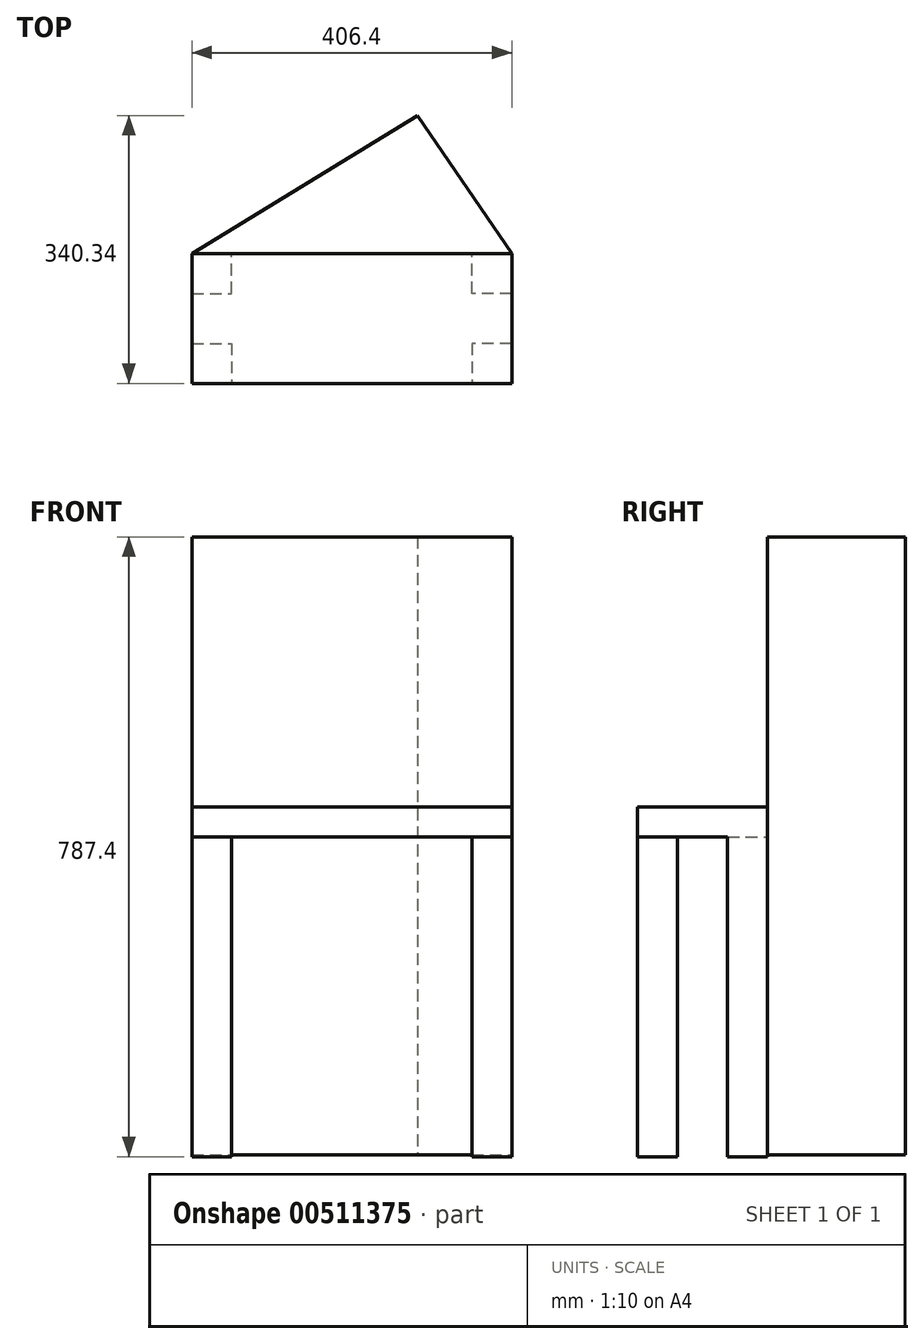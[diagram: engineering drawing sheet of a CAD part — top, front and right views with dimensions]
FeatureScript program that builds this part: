
annotation { "Feature Type Name" : "Feature", "Feature Type Description" : "" }
export const myFeature = defineFeature(function(context is Context, id is Id, definition is map)
    precondition{}
    {
        {
            var Q0;
            Q0=qCreatedBy(makeId("Top.planeOp"),FACE);
            var sketch = newSketch(context, id + "F0", { "sketchPlane" : qUnion([Q0])});
            skLineSegment(sketch, "E0", {"start": v(0, 0) * mm, "end": v(0, 50.8) * mm});
            skLineSegment(sketch, "E1", {"start": v(0, 50.8) * mm, "end": v(50.8, 50.8) * mm});
            skLineSegment(sketch, "E2", {"start": v(50.8, 50.8) * mm, "end": v(50.8, 0) * mm});
            skLineSegment(sketch, "E3", {"start": v(50.8, 0) * mm, "end": v(0, 0) * mm});
            skSolve(sketch);
        }
        {
            var Q0;
            Q0 = qSketchRegion(id + "F0", true);
            extrude(context, id + "F1", {"entities" : qUnion([Q0]), "depth" : 406.4 * mm});
        }
        {
            var Q0;
            Q0=makeQuery(id+"F1.opExtrude","CAP_FACE",FACE,{"disambiguationData":[OSD([sQuery(id+"F0.wireOp",EDGE,"E0"),sQuery(id+"F0.wireOp",EDGE,"E1"),sQuery(id+"F0.wireOp",EDGE,"E2"),sQuery(id+"F0.wireOp",EDGE,"E3")])],"isStart":false});
            var sketch = newSketch(context, id + "F2", { "sketchPlane" : qUnion([Q0])});
            skLineSegment(sketch, "E4", {"start": v(0, 0) * mm, "end": v(406.4, 0) * mm});
            skPoint(sketch, "E4.endSnap0", {"position": v(25.4, 0) * mm});
            skLineSegment(sketch, "E5", {"start": v(0, 0) * mm, "end": v(0, 164.9) * mm});
            skLineSegment(sketch, "E6", {"start": v(0, 164.9) * mm, "end": v(406.4, 164.9) * mm});
            skLineSegment(sketch, "E7", {"start": v(406.4, 164.9) * mm, "end": v(406.4, 0) * mm});
            skLineSegment(sketch, "E8", {"start": v(203.2, 164.9) * mm, "end": v(203.2, 0) * mm});
            skLineSegment(sketch, "E9", {"start": v(406.4, 82.45) * mm, "end": v(0, 82.45) * mm});
            skSolve(sketch);
        }
        {
            var Q0;
            Q0=sQuery(id+"F2.wireOp",EDGE,"E8");
            cPlane(context, id + "F3", {"entities" : qUnion([Q0]), "cplaneType" : CPlaneType.LINE_ANGLE, "offset" : 25.4 * mm, "angle" : 90 * degree, "width" : 152.4 * mm, "height" : 152.4 * mm});
        }
        {
            var Q0;
            Q0=sQuery(id+"F2.wireOp",EDGE,"E9");
            cPlane(context, id + "F4", {"entities" : qUnion([Q0]), "cplaneType" : CPlaneType.LINE_ANGLE, "offset" : 25.4 * mm, "angle" : 0 * degree, "width" : 152.4 * mm, "height" : 152.4 * mm});
        }
        {
            var Q0;
            Q0=makeQuery(id+"F1.opExtrude","SWEPT_BODY",BODY,{"disambiguationData":[OSD([sQuery(id+"F0.wireOp",EDGE,"E0"),sQuery(id+"F0.wireOp",EDGE,"E1"),sQuery(id+"F0.wireOp",EDGE,"E2"),sQuery(id+"F0.wireOp",EDGE,"E3")])]});
            var Q1;
            Q1=qCreatedBy(id+"F4.planeOp",FACE);
            mirror(context, id + "F5", {"entities" : qUnion([Q0]), "mirrorPlane" : qUnion([Q1])});
        }
        {
            var Q0;
            Q0=makeQuery(id+"F5.opPattern","COPY",BODY,{"derivedFrom":makeQuery(id+"F1.opExtrude","SWEPT_BODY",BODY,{"disambiguationData":[OSD([sQuery(id+"F0.wireOp",EDGE,"E0"),sQuery(id+"F0.wireOp",EDGE,"E1"),sQuery(id+"F0.wireOp",EDGE,"E2"),sQuery(id+"F0.wireOp",EDGE,"E3")])]}),"instanceName":"1"});
            var Q1;
            Q1=makeQuery(id+"F1.opExtrude","SWEPT_BODY",BODY,{"disambiguationData":[OSD([sQuery(id+"F0.wireOp",EDGE,"E0"),sQuery(id+"F0.wireOp",EDGE,"E1"),sQuery(id+"F0.wireOp",EDGE,"E2"),sQuery(id+"F0.wireOp",EDGE,"E3")])]});
            var Q2;
            Q2=qCreatedBy(id+"F3.planeOp",FACE);
            mirror(context, id + "F6", {"entities" : qUnion([Q0, Q1]), "mirrorPlane" : qUnion([Q2])});
        }
        {
            var Q0;
            {var subQ0=sQuery(id+"F2.wireOp",EDGE,"E7");var subQ1=sQuery(id+"F2.wireOp",EDGE,"E4");var subQ2=makeQuery(id+"F2.imprint","INTERSECT",VERTEX,{"derivedFrom":[subQ1,subQ0]});Q0=makeQuery(id+"F2.imprint","IMPRINT",FACE,{"disambiguationData":[TD([[makeQuery(id+"F2.imprint","IMPRINT",EDGE,{"disambiguationData":[TD([[subQ2,1.0]])],"derivedFrom":subQ1}),1.0]])]});}
            var Q1;
            {var subQ0=sQuery(id+"F2.wireOp",EDGE,"E6");var subQ1=sQuery(id+"F2.wireOp",EDGE,"E5");var subQ2=makeQuery(id+"F2.imprint","INTERSECT",VERTEX,{"derivedFrom":[subQ1,subQ0]});Q1=makeQuery(id+"F2.imprint","IMPRINT",FACE,{"disambiguationData":[TD([[makeQuery(id+"F2.imprint","IMPRINT",EDGE,{"disambiguationData":[TD([[subQ2,1.0]])],"derivedFrom":subQ1}),-1.0]])]});}
            var Q2;
            {var subQ5=makeQuery(id+"F1.opExtrude","CAP_EDGE",EDGE,{"disambiguationData":[OSD([sQuery(id+"F0.wireOp",EDGE,"E1")])],"isStart":false});Q2=makeQuery(id+"F2.imprint","IMPRINT",FACE,{"disambiguationData":[TD([[makeQuery(id+"F2.imprint","IMPRINT",EDGE,{"derivedFrom":subQ5}),1.0]])]});}
            var Q3;
            {var subQ0=sQuery(id+"F2.wireOp",EDGE,"E7");var subQ1=sQuery(id+"F2.wireOp",EDGE,"E6");var subQ2=makeQuery(id+"F2.imprint","INTERSECT",VERTEX,{"derivedFrom":[subQ1,subQ0]});Q3=makeQuery(id+"F2.imprint","IMPRINT",FACE,{"disambiguationData":[TD([[makeQuery(id+"F2.imprint","IMPRINT",EDGE,{"disambiguationData":[TD([[subQ2,1.0]])],"derivedFrom":subQ1}),-1.0]])]});}
            var Q4;
            {var subQ4=makeQuery(id+"F1.opExtrude","CAP_EDGE",EDGE,{"disambiguationData":[OSD([sQuery(id+"F0.wireOp",EDGE,"E1")])],"isStart":false});Q4=makeQuery(id+"F2.imprint","IMPRINT",FACE,{"disambiguationData":[TD([[makeQuery(id+"F2.imprint","IMPRINT",EDGE,{"derivedFrom":subQ4}),-1.0]])]});}
            extrude(context, id + "F7", {"entities" : qUnion([Q0, Q1, Q2, Q3, Q4]), "depth" : 38.1 * mm});
        }
        {
            var Q0;
            Q0=makeQuery(id+"F7.opExtrude","CAP_FACE",FACE,{"disambiguationData":[OSD([sQuery(id+"F2.wireOp",EDGE,"E4"),sQuery(id+"F2.wireOp",EDGE,"E5"),sQuery(id+"F2.wireOp",EDGE,"E6"),sQuery(id+"F2.wireOp",EDGE,"E7")])],"isStart":false});
            var sketch = newSketch(context, id + "F8", { "sketchPlane" : qUnion([Q0])});
            skLineSegment(sketch, "E10", {"start": v(0, 164.9) * mm, "end": v(286.76, 340.34) * mm});
            skLineSegment(sketch, "E11", {"start": v(286.76, 340.34) * mm, "end": v(406.4, 164.9) * mm});
            skLineSegment(sketch, "E12", {"start": v(406.4, 164.9) * mm, "end": v(0, 164.9) * mm});
            skSolve(sketch);
        }
        {
            var Q0;
            {var subQ3=sQuery(id+"F8.wireOp",EDGE,"KRt3QSpN-Ba8B-c9nY-8ort-uqdr8mKLbynd");Q0=makeQuery(id+"F8.imprint","IMPRINT",FACE,{"disambiguationData":[TD([[makeQuery(id+"F8.imprint","IMPRINT",EDGE,{"derivedFrom":subQ3}),-1.0]])]});}
            var Q1;
            {var subQ1=sQuery(id+"F8.wireOp",EDGE,"9oY8DTfp-ns2C-kw6H-IZ9c-m7aqdasaaiO2");var subQ3=makeQuery(id+"F7.opExtrude","CAP_EDGE",EDGE,{"disambiguationData":[OSD([sQuery(id+"F2.wireOp",EDGE,"E6")])],"isStart":false});var subQ4=makeQuery(id+"F8.imprint","INTERSECT",VERTEX,{"derivedFrom":[subQ3,subQ1]});Q1=makeQuery(id+"F8.imprint","IMPRINT",FACE,{"disambiguationData":[TD([[makeQuery(id+"F8.imprint","IMPRINT",EDGE,{"disambiguationData":[TD([[subQ4,-1.0]])],"derivedFrom":subQ3}),-1.0]])]});}
            var Q2;
            Q2=makeQuery(id+"F8.imprint","IMPRINT",FACE,{"disambiguationData":[TD([[makeQuery(id+"F8.imprint","IMPRINT",EDGE,{"derivedFrom":sQuery(id+"F8.wireOp",EDGE,"E10")}),-1.0]])]});
            extrude(context, id + "F9", {"entities" : qUnion([Q0, Q1, Q2]), "operationType" : NewBodyOperationType.ADD, "depth" : 342.9 * mm, "hasSecondDirection" : true, "secondDirectionOppositeDirection" : true, "secondDirectionDepth" : 441.96 * mm});
        }
    });
